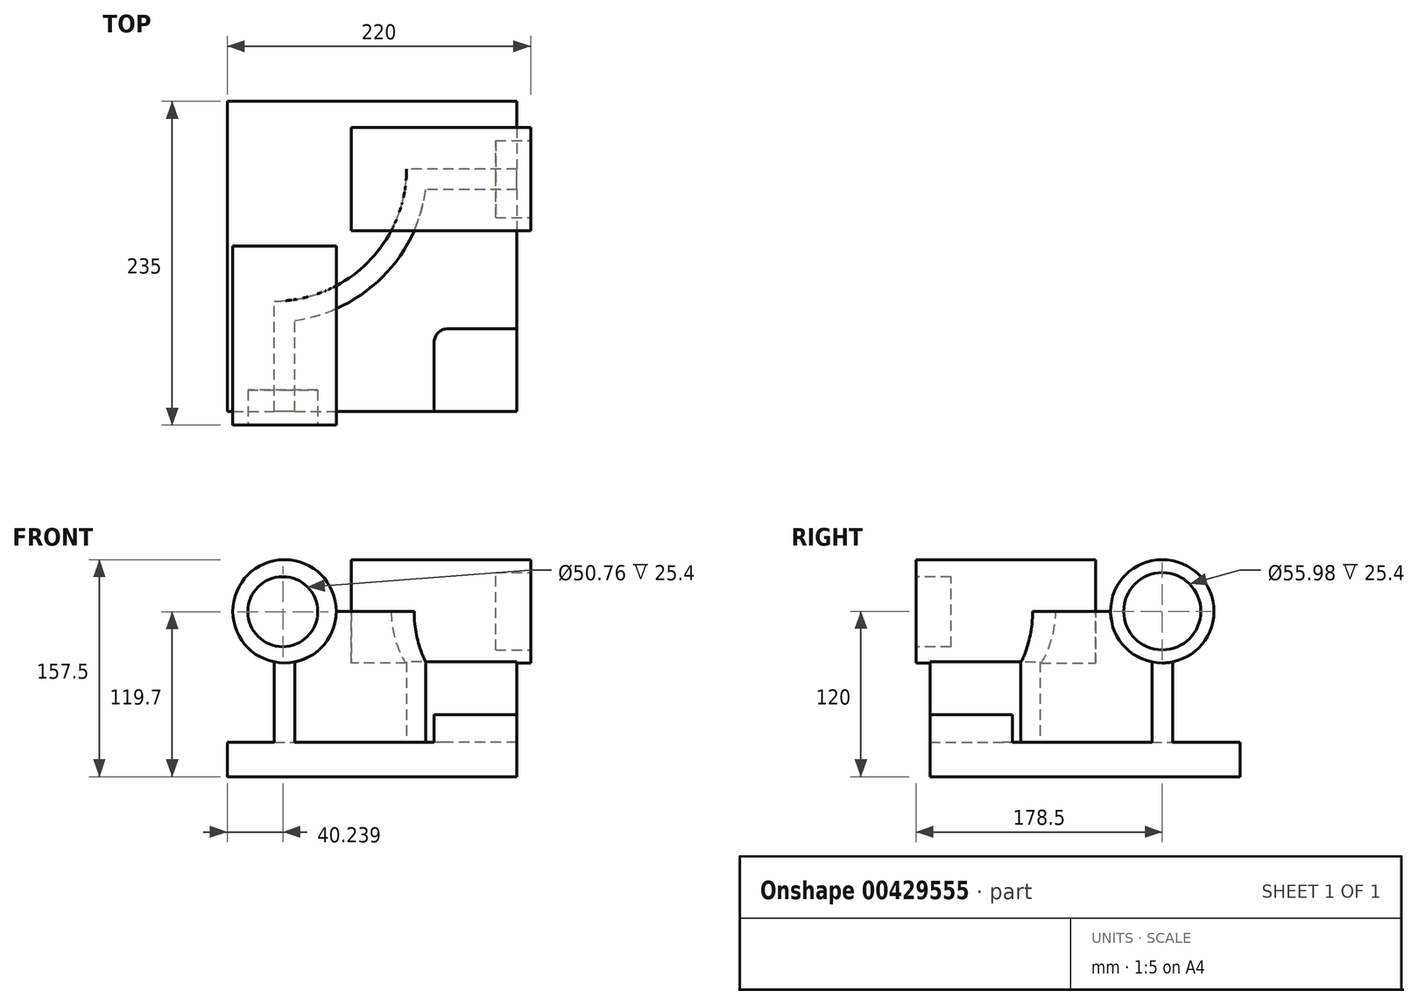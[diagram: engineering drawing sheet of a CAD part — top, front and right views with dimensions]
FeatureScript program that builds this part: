
annotation { "Feature Type Name" : "Feature", "Feature Type Description" : "" }
export const myFeature = defineFeature(function(context is Context, id is Id, definition is map)
    precondition{}
    {
        {
            var Q0;
            Q0=qCreatedBy(makeId("Top.planeOp"),FACE);
            var sketch = newSketch(context, id + "F0", { "sketchPlane" : qUnion([Q0])});
            skLineSegment(sketch, "E0.bottom", {"start": v(-105, 112.5) * mm, "end": v(105, 112.5) * mm});
            skLineSegment(sketch, "E0.top", {"start": v(-105, -112.5) * mm, "end": v(105, -112.5) * mm});
            skLineSegment(sketch, "E0.left", {"start": v(-105, 112.5) * mm, "end": v(-105, -112.5) * mm});
            skLineSegment(sketch, "E0.right", {"start": v(105, 112.5) * mm, "end": v(105, -112.5) * mm});
            skPoint(sketch, "E0.middle", {"position": v(0, 0) * mm});
            skSolve(sketch);
        }
        {
            var Q0;
            Q0=makeQuery(id+"F0.imprint","IMPRINT",FACE,{"disambiguationData":[TD([[makeQuery(id+"F0.imprint","IMPRINT",EDGE,{"derivedFrom":sQuery(id+"F0.wireOp",EDGE,"E0.bottom")}),-1.0]])]});
            extrude(context, id + "F1", {"entities" : qUnion([Q0]), "depth" : 25 * mm});
        }
        {
            var Q0;
            Q0=makeQuery(id+"F1.opExtrude","CAP_FACE",FACE,{"disambiguationData":[OSD([sQuery(id+"F0.wireOp",EDGE,"E0.bottom"),sQuery(id+"F0.wireOp",EDGE,"E0.top"),sQuery(id+"F0.wireOp",EDGE,"E0.left"),sQuery(id+"F0.wireOp",EDGE,"E0.right")])],"isStart":false});
            var sketch = newSketch(context, id + "F2", { "sketchPlane" : qUnion([Q0])});
            skLineSegment(sketch, "E1", {"start": v(-71, -112.5) * mm, "end": v(-71, -32.5) * mm});
            skLineSegment(sketch, "E2", {"start": v(105, 63.5) * mm, "end": v(25, 63.5) * mm});
            skArc(sketch, "E3", {"start": v(-71, -32.5) * mm, "mid": v(-3.12, -4.38) * mm, "end": v(25, 63.5) * mm});
            skLineSegment(sketch, "E4", {"start": v(-71, 63.5) * mm, "end": v(-71, -32.5) * mm, "construction": true});
            skLineSegment(sketch, "E5", {"start": v(-71, 63.5) * mm, "end": v(25, 63.5) * mm, "construction": true});
            skLineSegment(sketch, "E6.0", {"start": v(-56, -112.5) * mm, "end": v(-56, -46.48) * mm});
            skArc(sketch, "E6.1", {"start": v(-56, -46.48) * mm, "mid": v(7.49, -14.99) * mm, "end": v(38.98, 48.5) * mm});
            skLineSegment(sketch, "E6.2", {"start": v(105, 48.5) * mm, "end": v(38.98, 48.5) * mm});
            skLineSegment(sketch, "E7.0", {"start": v(105, 112.5) * mm, "end": v(105, -112.5) * mm});
            skLineSegment(sketch, "E8.0", {"start": v(-105, -112.5) * mm, "end": v(105, -112.5) * mm});
            skSolve(sketch);
        }
        {
            var Q0;
            {var subQ2=sQuery(id+"F2.wireOp",EDGE,"E1");Q0=makeQuery(id+"F2.imprint","IMPRINT",FACE,{"disambiguationData":[TD([[makeQuery(id+"F2.imprint","IMPRINT",EDGE,{"derivedFrom":subQ2}),-1.0]])]});}
            extrude(context, id + "F3", {"entities" : qUnion([Q0]), "operationType" : NewBodyOperationType.ADD, "depth" : 95 * mm});
        }
        {
            var Q0;
            Q0=makeQuery(id+"F3.boolean.opBoolean","MERGE",FACE,{"derivedFrom":[makeQuery(id+"F1.opExtrude","SWEPT_FACE",FACE,{"disambiguationData":[OSD([sQuery(id+"F0.wireOp",EDGE,"E0.top")])]}),makeQuery(id+"F3.opExtrude","SWEPT_FACE",FACE,{"disambiguationData":[OSD([sQuery(id+"F2.wireOp",EDGE,"E8.0")])]})]});
            var sketch = newSketch(context, id + "F4", { "sketchPlane" : qUnion([Q0])});
            skCircle(sketch, "E9", {"center": v(-63.5, 120) * mm, "radius": 37.5 * mm});
            skSolve(sketch);
        }
        {
            var Q0;
            {var subQ1=sQuery(id+"F2.wireOp",EDGE,"E8.0");var subQ6=makeQuery(id+"F3.opExtrude","CAP_EDGE",EDGE,{"disambiguationData":[OSD([subQ1])],"isStart":false});Q0=makeQuery(id+"F4.imprint","IMPRINT",FACE,{"disambiguationData":[TD([[makeQuery(id+"F4.imprint","IMPRINT",EDGE,{"derivedFrom":subQ6}),1.0]])]});}
            var Q1;
            {var subQ1=sQuery(id+"F2.wireOp",EDGE,"E8.0");var subQ6=makeQuery(id+"F3.opExtrude","CAP_EDGE",EDGE,{"disambiguationData":[OSD([subQ1])],"isStart":false});Q1=makeQuery(id+"F4.imprint","IMPRINT",FACE,{"disambiguationData":[TD([[makeQuery(id+"F4.imprint","IMPRINT",EDGE,{"derivedFrom":subQ6}),-1.0]])]});}
            extrude(context, id + "F5", {"entities" : qUnion([Q0, Q1]), "operationType" : NewBodyOperationType.ADD, "depth" : 10 * mm, "hasSecondDirection" : true, "secondDirectionOppositeDirection" : true, "secondDirectionDepth" : 120 * mm});
        }
        {
            var Q0;
            Q0=makeQuery(id+"F3.boolean.opBoolean","MERGE",FACE,{"derivedFrom":[makeQuery(id+"F1.opExtrude","SWEPT_FACE",FACE,{"disambiguationData":[OSD([sQuery(id+"F0.wireOp",EDGE,"E0.right")])]}),makeQuery(id+"F3.opExtrude","SWEPT_FACE",FACE,{"disambiguationData":[OSD([sQuery(id+"F2.wireOp",EDGE,"E7.0")])]})]});
            var sketch = newSketch(context, id + "F6", { "sketchPlane" : qUnion([Q0])});
            skCircle(sketch, "E10", {"center": v(56, 120) * mm, "radius": 37.5 * mm});
            skSolve(sketch);
        }
        {
            var Q0;
            {var subQ1=sQuery(id+"F2.wireOp",EDGE,"E7.0");var subQ6=makeQuery(id+"F3.opExtrude","CAP_EDGE",EDGE,{"disambiguationData":[OSD([subQ1])],"isStart":false});Q0=makeQuery(id+"F6.imprint","IMPRINT",FACE,{"disambiguationData":[TD([[makeQuery(id+"F6.imprint","IMPRINT",EDGE,{"derivedFrom":subQ6}),1.0]])]});}
            var Q1;
            {var subQ1=sQuery(id+"F2.wireOp",EDGE,"E7.0");var subQ6=makeQuery(id+"F3.opExtrude","CAP_EDGE",EDGE,{"disambiguationData":[OSD([subQ1])],"isStart":false});Q1=makeQuery(id+"F6.imprint","IMPRINT",FACE,{"disambiguationData":[TD([[makeQuery(id+"F6.imprint","IMPRINT",EDGE,{"derivedFrom":subQ6}),-1.0]])]});}
            extrude(context, id + "F7", {"entities" : qUnion([Q0, Q1]), "operationType" : NewBodyOperationType.ADD, "depth" : 10 * mm, "hasSecondDirection" : true, "secondDirectionOppositeDirection" : true, "secondDirectionDepth" : 120 * mm});
        }
        {
            var Q0;
            {var subQ0=sQuery(id+"F0.wireOp",EDGE,"E0.left");var subQ1=sQuery(id+"F0.wireOp",EDGE,"E0.top");var subQ2=sQuery(id+"F0.wireOp",EDGE,"E0.right");var subQ3=sQuery(id+"F0.wireOp",EDGE,"E0.bottom");Q0=makeQuery(id+"F3.boolean.opBoolean","SPLIT",FACE,{"disambiguationData":[TD([makeQuery(id+"F1.opExtrude","SWEPT_FACE",FACE,{"disambiguationData":[OSD([subQ3])]})])],"derivedFrom":makeQuery(id+"F1.opExtrude","CAP_FACE",FACE,{"disambiguationData":[OSD([subQ3,subQ1,subQ0,subQ2])],"isStart":false})});}
            var sketch = newSketch(context, id + "F8", { "sketchPlane" : qUnion([Q0])});
            skLineSegment(sketch, "E11.bottom", {"start": v(105, -112.5) * mm, "end": v(45, -112.5) * mm});
            skLineSegment(sketch, "E11.top", {"start": v(105, -52.5) * mm, "end": v(45, -52.5) * mm});
            skLineSegment(sketch, "E11.left", {"start": v(105, -112.5) * mm, "end": v(105, -52.5) * mm});
            skLineSegment(sketch, "E11.right", {"start": v(45, -112.5) * mm, "end": v(45, -52.5) * mm});
            skSolve(sketch);
        }
        {
            var Q0;
            Q0=makeQuery(id+"F8.imprint","IMPRINT",FACE,{"disambiguationData":[TD([[makeQuery(id+"F8.imprint","IMPRINT",EDGE,{"derivedFrom":sQuery(id+"F8.wireOp",EDGE,"E11.bottom")}),-1.0]])]});
            extrude(context, id + "F9", {"entities" : qUnion([Q0]), "operationType" : NewBodyOperationType.ADD, "depth" : 20 * mm});
        }
        {
            var Q0;
            Q0=makeQuery(id+"F9.opExtrude","SWEPT_EDGE",EDGE,{"disambiguationData":[OSD([sQuery(id+"F8.wireOp",EDGE,"E11.top"),sQuery(id+"F8.wireOp",EDGE,"E11.right")])]});
            fillet(context, id + "F10", {"entities" : qUnion([Q0]), "radius" : 10 * mm, "tangentPropagation" : true, "allowEdgeOverflow" : false});
        }
        {
            var Q0;
            Q0=makeQuery(id+"F5.opExtrude","CAP_FACE",FACE,{"disambiguationData":[OSD([sQuery(id+"F4.wireOp",EDGE,"E9")])],"isStart":false});
            var sketch = newSketch(context, id + "F11", { "sketchPlane" : qUnion([Q0])});
            skSolve(sketch);
        }
        {
            var Q0;
            Q0=makeQuery(id+"F11.imprint","IMPRINT",FACE,{"disambiguationData":[TD([[makeQuery(id+"F11.imprint","IMPRINT",EDGE,{"derivedFrom":makeQuery(id+"F5.opExtrude","CAP_EDGE",EDGE,{"disambiguationData":[OSD([sQuery(id+"F4.wireOp",EDGE,"E9")])],"isStart":false})}),1.0]])]});
            var sketch = newSketch(context, id + "F12", { "sketchPlane" : qUnion([Q0])});
            skCircle(sketch, "E12", {"center": v(-64.76, 119.7) * mm, "radius": 25.38 * mm});
            skSolve(sketch);
        }
        {
            var Q0;
            Q0 = qSketchRegion(id + "F12", true);
            extrude(context, id + "F13", {"entities" : qUnion([Q0]), "operationType" : NewBodyOperationType.REMOVE, "oppositeDirection" : true, "depth" : 25.4 * mm, "offsetDistance" : 25.4 * mm});
        }
        {
            var Q0;
            Q0=makeQuery(id+"F7.opExtrude","CAP_FACE",FACE,{"disambiguationData":[OSD([sQuery(id+"F6.wireOp",EDGE,"E10")])],"isStart":false});
            var sketch = newSketch(context, id + "F14", { "sketchPlane" : qUnion([Q0])});
            skCircle(sketch, "E13", {"center": v(56, 120) * mm, "radius": 28 * mm});
            skSolve(sketch);
        }
        {
            var Q0;
            Q0 = qSketchRegion(id + "F14", true);
            extrude(context, id + "F15", {"entities" : qUnion([Q0]), "operationType" : NewBodyOperationType.REMOVE, "oppositeDirection" : true, "depth" : 25.4 * mm, "offsetDistance" : 25.4 * mm});
        }
    });
